# Revit family: 25V
name_source: partatom
category: Specialty Equipment
units: mm (PartAtom-declared; Revit-internal decimal feet)

## family parameters
Cut with Voids When Loaded = No
Host = Face
Part Type = Normal
Room Calculation Point = No
Round Connector Dimension = Use Diameter
Shared = No

## types (18) — shared parameters
ABAA Compliance = No
Assembly Code = C3020200
Default Elevation = 0"
Description = Primary seal in masonry where black reveal or shadow-line effect is desired
Manufacturer = EMSEAL Joint Systems Ltd
Model = 25V
Movement (of Nominal Material Size) = +25% / -25%
Pick Resistance = No
Product Data URL = https://bit.ly
Product Documentation URL = https://bit.ly
Product Page URL = https://bit.ly
R Value Range (ASTM C518) = 2.1 per 1-inch (25mm) depth
Rate of Air Leakage (ASTM E283) = Passed
Staining (ASTM C510) = None
Temperature Range (ASTM C711) = 185°F (85°C) to -40°F (-40°C)
Tensile Strength (ASTM D3574) = 21 psi min; 145 kPa
Type Image = EMSEAL-25V.jpg
URL = http://www.emseal.com

## per-type parameters (varying)
| type | Depth | Width |
| 25V - .25 inches | 3/4" | 1/4" |
| 25V - .325 inches | 3/4" | 83/256" |
| 25V - .5 inches | 3/4" | 1/2" |
| 25V - .625 inches | 1" | 5/8" |
| 25V - .75 inches | 1" | 3/4" |
| 25V - 1 inches | 1 1/2" | 1" |
| 25V - 1.25 inches | 2" | 1 1/4" |
| 25V - 1.5 inches | 2" | 1 1/2" |
| 25V - 1.75 inches | 2" | 1 3/4" |
| 25V - 2 inches | 2 1/2" | 2" |
| 25V - 2.25 inches | 2 1/2" | 2 1/4" |
| 25V - 2.5 inches | 2 3/4" | 2 1/2" |
| 25V - 2.75 inches | 3" | 2 3/4" |
| 25V - 3 inches | 3" | 3" |
| 25V - 3.25 inches | 3 1/2" | 3 1/4" |
| 25V - 3.5 inches | 3 1/2" | 3 1/2" |
| 25V - 3.75 inches | 4" | 3 3/4" |
| 25V - 4 inches | 4" | 4" |

## geometry (parser evidence)
native form markers: Sweep x3
no freeform markers — native parametric forms only
